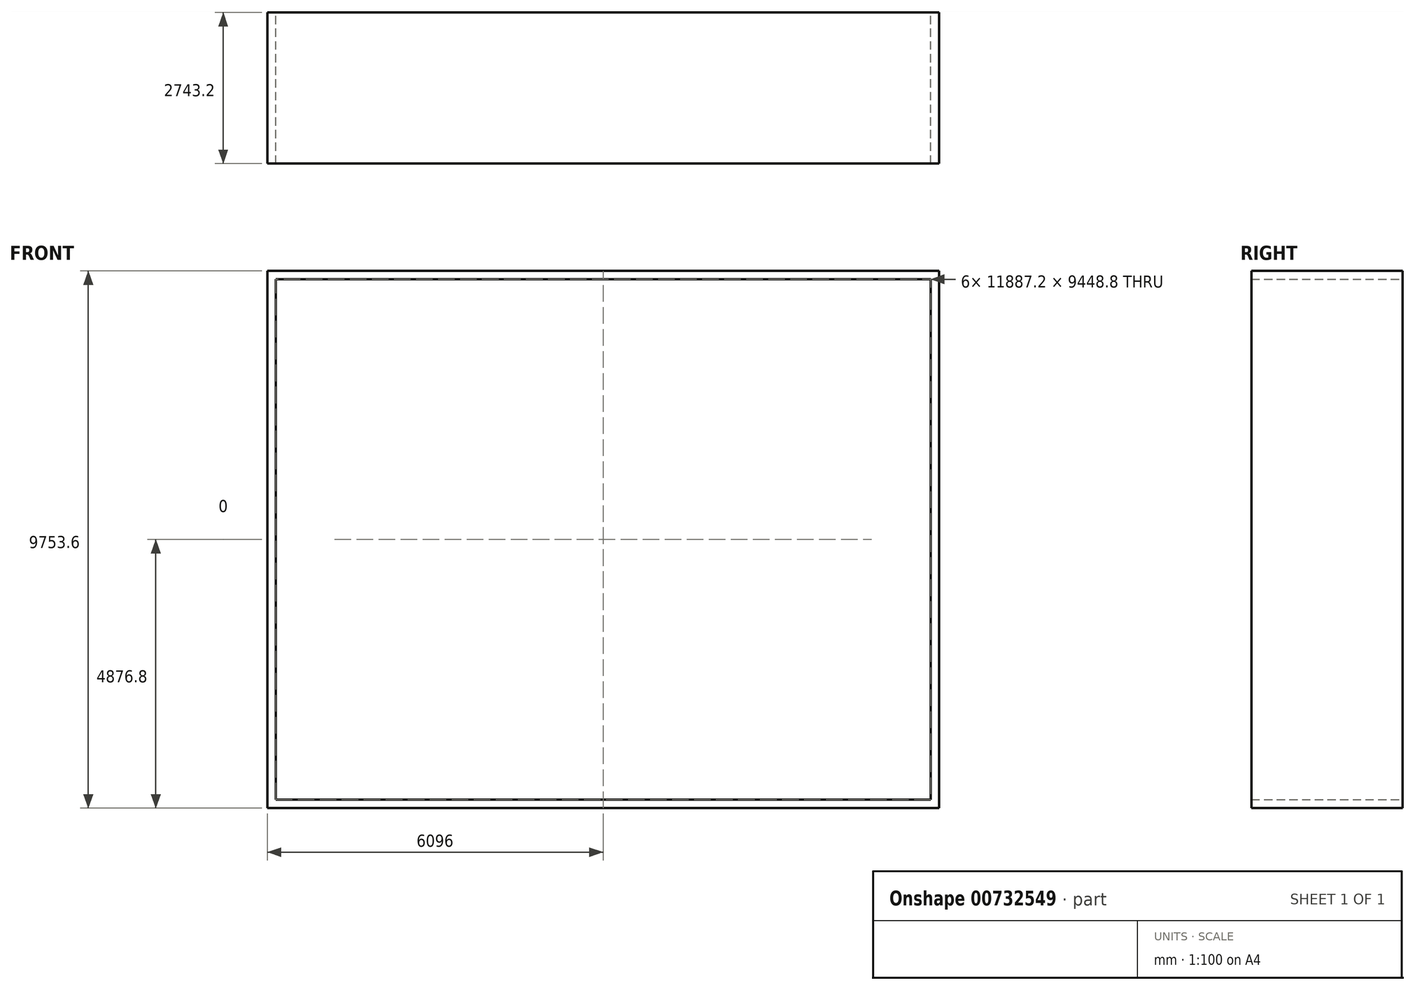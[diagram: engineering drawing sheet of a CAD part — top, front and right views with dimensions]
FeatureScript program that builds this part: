
annotation { "Feature Type Name" : "Feature", "Feature Type Description" : "" }
export const myFeature = defineFeature(function(context is Context, id is Id, definition is map)
    precondition{}
    {
        {
            var Q0;
            Q0=qCreatedBy(makeId("Front.planeOp"),FACE);
            var sketch = newSketch(context, id + "F0", { "sketchPlane" : qUnion([Q0])});
            skLineSegment(sketch, "E0.bottom", {"start": v(88.7, 9560.63) * mm, "end": v(11975.9, 9560.63) * mm});
            skLineSegment(sketch, "E0.top", {"start": v(88.7, 111.83) * mm, "end": v(11975.9, 111.83) * mm});
            skLineSegment(sketch, "E0.left", {"start": v(88.7, 9560.63) * mm, "end": v(88.7, 111.83) * mm});
            skLineSegment(sketch, "E0.right", {"start": v(11975.9, 9560.63) * mm, "end": v(11975.9, 111.83) * mm});
            skLineSegment(sketch, "E1.0", {"start": v(-63.7, 9713.03) * mm, "end": v(12128.3, 9713.03) * mm});
            skLineSegment(sketch, "E1.1", {"start": v(-63.7, 9713.03) * mm, "end": v(-63.7, -40.57) * mm});
            skLineSegment(sketch, "E1.2", {"start": v(-63.7, -40.57) * mm, "end": v(12128.3, -40.57) * mm});
            skLineSegment(sketch, "E1.3", {"start": v(12128.3, 9713.03) * mm, "end": v(12128.3, -40.57) * mm});
            skSolve(sketch);
        }
        {
            var Q0;
            Q0 = qSketchRegion(id + "F0", true);
            extrude(context, id + "F1", {"entities" : qUnion([Q0]), "depth" : 2743.2 * mm, "offsetDistance" : 25.4 * mm});
        }
    });
